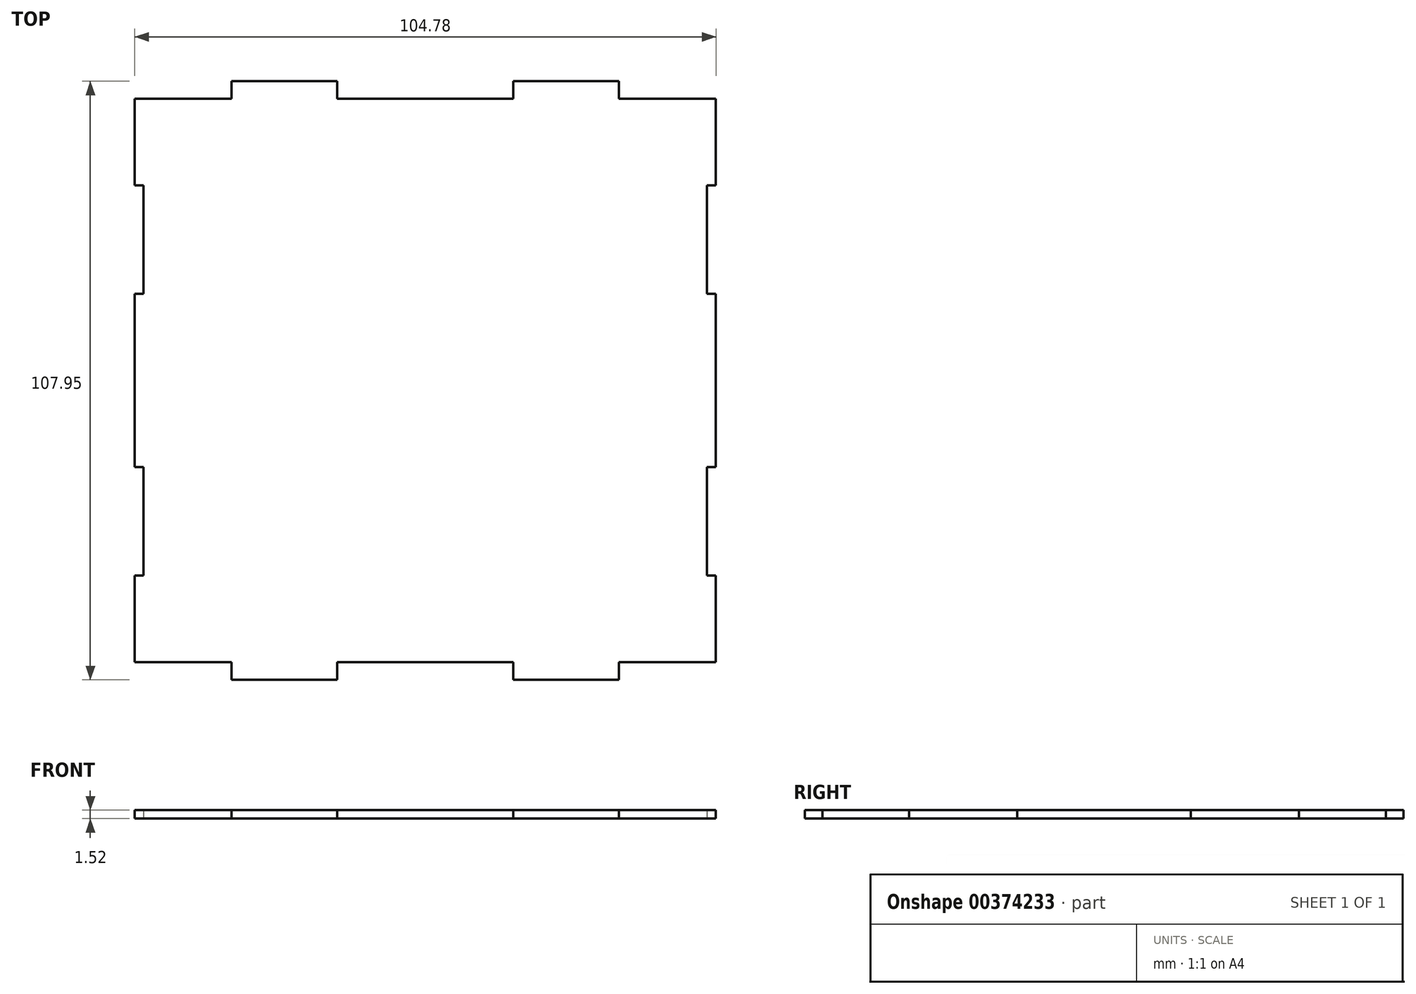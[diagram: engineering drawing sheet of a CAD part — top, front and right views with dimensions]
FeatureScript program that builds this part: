
annotation { "Feature Type Name" : "Feature", "Feature Type Description" : "" }
export const myFeature = defineFeature(function(context is Context, id is Id, definition is map)
    precondition{}
    {
        {
            var Q0;
            Q0=qCreatedBy(makeId("Top.planeOp"),FACE);
            var sketch = newSketch(context, id + "F0", { "sketchPlane" : qUnion([Q0])});
            skLineSegment(sketch, "E0", {"start": v(41.2, -61.91) * mm, "end": v(58.65, -61.91) * mm});
            skLineSegment(sketch, "E1", {"start": v(145.97, -61.91) * mm, "end": v(145.97, -46.3) * mm});
            skLineSegment(sketch, "E2", {"start": v(145.97, -46.3) * mm, "end": v(144.38, -46.3) * mm});
            skLineSegment(sketch, "E3", {"start": v(144.38, -46.3) * mm, "end": v(144.38, -26.73) * mm});
            skLineSegment(sketch, "E4", {"start": v(144.38, -26.73) * mm, "end": v(145.97, -26.73) * mm});
            skLineSegment(sketch, "E5", {"start": v(145.97, -26.73) * mm, "end": v(145.97, 4.5) * mm});
            skLineSegment(sketch, "E6", {"start": v(145.97, 4.5) * mm, "end": v(144.38, 4.5) * mm});
            skLineSegment(sketch, "E7", {"start": v(144.38, 4.5) * mm, "end": v(144.38, 24.07) * mm});
            skLineSegment(sketch, "E8", {"start": v(144.38, 24.07) * mm, "end": v(145.97, 24.07) * mm});
            skLineSegment(sketch, "E9", {"start": v(145.97, 24.07) * mm, "end": v(145.97, 39.69) * mm});
            skLineSegment(sketch, "E10", {"start": v(145.97, 39.69) * mm, "end": v(128.5, 39.69) * mm});
            skLineSegment(sketch, "E11", {"start": v(41.2, 39.69) * mm, "end": v(41.2, 24.07) * mm});
            skLineSegment(sketch, "E12", {"start": v(41.2, 24.07) * mm, "end": v(42.78, 24.07) * mm});
            skLineSegment(sketch, "E13", {"start": v(42.78, 24.07) * mm, "end": v(42.78, 4.5) * mm});
            skLineSegment(sketch, "E14", {"start": v(42.78, 4.5) * mm, "end": v(41.2, 4.5) * mm});
            skLineSegment(sketch, "E15", {"start": v(41.2, 4.5) * mm, "end": v(41.2, -26.73) * mm});
            skLineSegment(sketch, "E16", {"start": v(41.2, -26.73) * mm, "end": v(42.78, -26.73) * mm});
            skLineSegment(sketch, "E17", {"start": v(42.78, -26.73) * mm, "end": v(42.78, -46.3) * mm});
            skLineSegment(sketch, "E18", {"start": v(42.78, -46.3) * mm, "end": v(41.2, -46.3) * mm});
            skLineSegment(sketch, "E19", {"start": v(41.2, -46.3) * mm, "end": v(41.2, -61.91) * mm});
            skLineSegment(sketch, "E20", {"start": v(58.65, -65.09) * mm, "end": v(77.7, -65.09) * mm});
            skLineSegment(sketch, "E21", {"start": v(77.7, -65.09) * mm, "end": v(77.7, -61.91) * mm});
            skLineSegment(sketch, "E22", {"start": v(58.65, -61.91) * mm, "end": v(58.65, -65.09) * mm});
            skLineSegment(sketch, "E23", {"start": v(128.5, -65.09) * mm, "end": v(109.45, -65.09) * mm});
            skLineSegment(sketch, "E24", {"start": v(109.45, -65.09) * mm, "end": v(109.45, -61.91) * mm});
            skLineSegment(sketch, "E25", {"start": v(128.5, -61.91) * mm, "end": v(128.5, -65.09) * mm});
            skLineSegment(sketch, "E26", {"start": v(77.7, -61.91) * mm, "end": v(109.45, -61.91) * mm});
            skLineSegment(sketch, "E27", {"start": v(128.5, -61.91) * mm, "end": v(145.97, -61.91) * mm});
            skLineSegment(sketch, "E28", {"start": v(58.65, 42.86) * mm, "end": v(77.7, 42.86) * mm});
            skLineSegment(sketch, "E29", {"start": v(77.7, 42.86) * mm, "end": v(77.7, 39.69) * mm});
            skLineSegment(sketch, "E30", {"start": v(58.65, 39.69) * mm, "end": v(58.65, 42.86) * mm});
            skLineSegment(sketch, "E31", {"start": v(128.5, 42.86) * mm, "end": v(109.45, 42.86) * mm});
            skLineSegment(sketch, "E32", {"start": v(109.45, 42.86) * mm, "end": v(109.45, 39.69) * mm});
            skLineSegment(sketch, "E33", {"start": v(128.5, 39.69) * mm, "end": v(128.5, 42.86) * mm});
            skLineSegment(sketch, "E34", {"start": v(77.7, 39.69) * mm, "end": v(109.45, 39.69) * mm});
            skLineSegment(sketch, "E35", {"start": v(58.65, 39.69) * mm, "end": v(41.2, 39.69) * mm});
            skSolve(sketch);
        }
        {
            var Q0;
            Q0=makeQuery(id+"F0.imprint","IMPRINT",FACE,{"disambiguationData":[TD([[makeQuery(id+"F0.imprint","IMPRINT",EDGE,{"derivedFrom":sQuery(id+"F0.wireOp",EDGE,"E0")}),1.0]])]});
            extrude(context, id + "F1", {"entities" : qUnion([Q0]), "depth" : 1.52 * mm});
        }
    });
